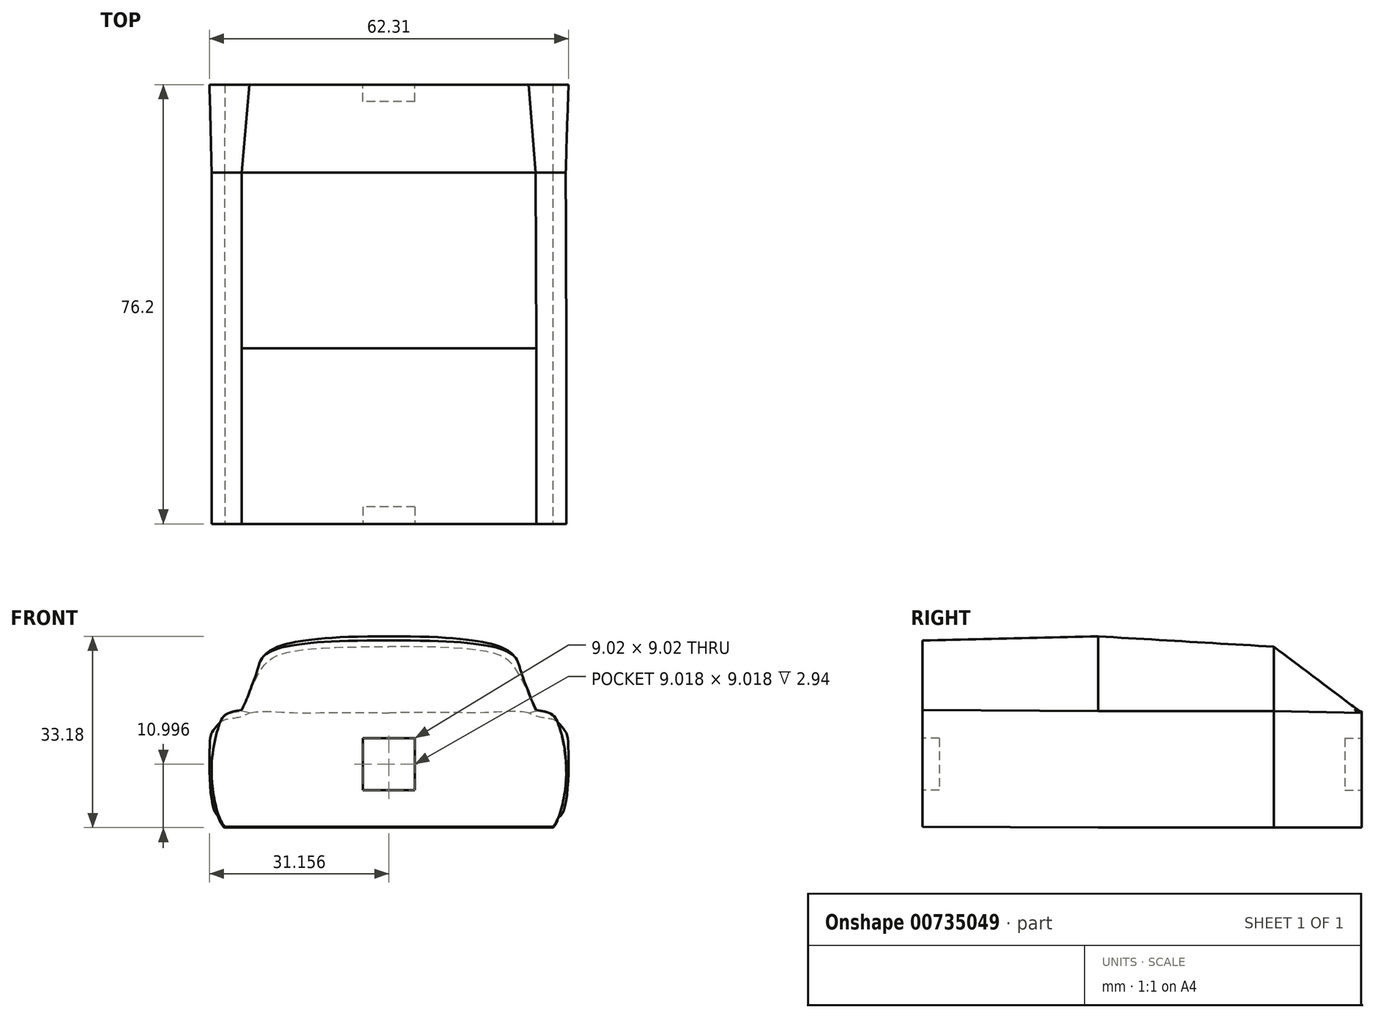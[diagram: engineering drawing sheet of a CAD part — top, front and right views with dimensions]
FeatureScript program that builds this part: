
annotation { "Feature Type Name" : "Feature", "Feature Type Description" : "" }
export const myFeature = defineFeature(function(context is Context, id is Id, definition is map)
    precondition{}
    {
        {
            var Q0;
            Q0=qCreatedBy(makeId("Front.planeOp"),FACE);
            var sketch = newSketch(context, id + "F0", { "sketchPlane" : qUnion([Q0])});
            skLineSegment(sketch, "E0", {"start": v(0, -183.1) * mm, "end": v(448.71, -183.1) * mm});
            skLineSegment(sketch, "E1", {"start": v(0, 369.77) * mm, "end": v(0, -183.1) * mm});
            skFitSpline(sketch, "E2", {"points": [v(448.71, -183.1) * mm, v(474.16, -183.1) * mm, v(512.73, -32.97) * mm, v(489.93, 114.17) * mm, v(425.94, 154.21) * mm], "startDerivative": vector(218.59, -88.61) * mm, "endDerivative": vector(-639.63, 77.65) * mm});
            skFitSpline(sketch, "E3", {"points": [v(425.94, 154.21) * mm, v(403.5, 206.57) * mm, v(378.22, 275.5) * mm, v(362.13, 312.27) * mm, v(0, 369.77) * mm], "startDerivative": vector(-217.52, 427.03) * mm, "endDerivative": vector(-1727.63, -7.94) * mm});
            skFitSpline(sketch, "E4.MirrorCS", {"points": [v(-448.71, -183.1) * mm, v(-474.16, -183.1) * mm, v(-512.73, -32.97) * mm, v(-489.93, 114.17) * mm, v(-425.94, 154.21) * mm], "startDerivative": vector(-218.59, -88.61) * mm, "endDerivative": vector(639.63, 77.65) * mm});
            skLineSegment(sketch, "E5.MirrorCS", {"start": v(0, -183.1) * mm, "end": v(-448.71, -183.1) * mm});
            skFitSpline(sketch, "E6.MirrorCS", {"points": [v(-425.94, 154.21) * mm, v(-403.5, 206.57) * mm, v(-378.22, 275.5) * mm, v(-362.13, 312.27) * mm, v(0, 369.77) * mm], "startDerivative": vector(217.52, 427.03) * mm, "endDerivative": vector(1727.63, -7.94) * mm});
            skLineSegment(sketch, "E7", {"start": v(-474.16, -183.1) * mm, "end": v(-448.71, -183.1) * mm});
            skLineSegment(sketch, "E8", {"start": v(448.71, -183.1) * mm, "end": v(474.16, -183.1) * mm});
            skSolve(sketch);
        }
        {
            var Q0;
            Q0=qCreatedBy(makeId("Front.planeOp"),FACE);
            cPlane(context, id + "F1", {"entities" : qUnion([Q0]), "cplaneType" : CPlaneType.OFFSET, "offset" : 508 * mm, "width" : 152.4 * mm, "height" : 152.4 * mm});
        }
        {
            var Q0;
            Q0=qCreatedBy(makeId("Front.planeOp"),FACE);
            cPlane(context, id + "F2", {"entities" : qUnion([Q0]), "cplaneType" : CPlaneType.OFFSET, "offset" : 508 * mm, "oppositeDirection" : true, "width" : 152.4 * mm, "height" : 152.4 * mm});
        }
        {
            var Q0;
            Q0=qCreatedBy(id+"F2.planeOp",FACE);
            var sketch = newSketch(context, id + "F3", { "sketchPlane" : qUnion([Q0])});
            skLineSegment(sketch, "E9", {"start": v(-0.85, -183.1) * mm, "end": v(447, -183.1) * mm});
            skLineSegment(sketch, "E10", {"start": v(-0.85, 339.88) * mm, "end": v(-0.85, -183.1) * mm});
            skFitSpline(sketch, "E11", {"points": [v(447, -183.1) * mm, v(474.16, -183.1) * mm, v(511.02, -32.97) * mm, v(488.22, 114.17) * mm, v(424.23, 154.21) * mm], "startDerivative": vector(218.59, -88.61) * mm, "endDerivative": vector(-639.63, 77.65) * mm});
            skFitSpline(sketch, "E12", {"points": [v(424.23, 154.21) * mm, v(401.78, 206.57) * mm, v(379.75, 253.63) * mm, v(351.9, 293.8) * mm, v(-0.85, 339.88) * mm], "startDerivative": vector(-217.52, 427.03) * mm, "endDerivative": vector(-1727.63, -7.94) * mm});
            skFitSpline(sketch, "E13.MirrorCS", {"points": [v(-448.71, -183.1) * mm, v(-475.87, -183.1) * mm, v(-512.73, -32.97) * mm, v(-489.93, 114.17) * mm, v(-425.94, 154.21) * mm], "startDerivative": vector(-218.59, -88.61) * mm, "endDerivative": vector(639.63, 77.65) * mm});
            skLineSegment(sketch, "E14.MirrorCS", {"start": v(-0.85, -183.1) * mm, "end": v(-448.71, -183.1) * mm});
            skFitSpline(sketch, "E15.MirrorCS", {"points": [v(-425.94, 154.21) * mm, v(-403.5, 206.57) * mm, v(-381.46, 253.63) * mm, v(-353.6, 293.8) * mm, v(-0.85, 339.88) * mm], "startDerivative": vector(217.52, 427.03) * mm, "endDerivative": vector(1727.63, -7.94) * mm});
            skLineSegment(sketch, "E16", {"start": v(-475.87, -183.1) * mm, "end": v(-448.71, -183.1) * mm});
            skLineSegment(sketch, "E17", {"start": v(447, -183.1) * mm, "end": v(474.16, -183.1) * mm});
            skSolve(sketch);
        }
        {
            var Q0;
            Q0=qCreatedBy(id+"F1.planeOp",FACE);
            var sketch = newSketch(context, id + "F4", { "sketchPlane" : qUnion([Q0])});
            skLineSegment(sketch, "E18", {"start": v(0, -180.47) * mm, "end": v(448.71, -180.47) * mm});
            skLineSegment(sketch, "E19", {"start": v(0, 357.9) * mm, "end": v(0, -180.47) * mm});
            skFitSpline(sketch, "E20", {"points": [v(448.71, -180.47) * mm, v(474.16, -180.47) * mm, v(512.73, -30.33) * mm, v(489.93, 116.8) * mm, v(425.94, 156.85) * mm], "startDerivative": vector(218.59, -88.61) * mm, "endDerivative": vector(-639.63, 77.65) * mm});
            skFitSpline(sketch, "E21", {"points": [v(425.94, 156.85) * mm, v(403.5, 209.2) * mm, v(380.6, 271.65) * mm, v(367.32, 306.69) * mm, v(0, 357.9) * mm], "startDerivative": vector(-217.52, 427.03) * mm, "endDerivative": vector(-1727.63, -7.94) * mm});
            skFitSpline(sketch, "E22.MirrorCS", {"points": [v(-448.71, -180.47) * mm, v(-474.16, -180.47) * mm, v(-512.73, -30.33) * mm, v(-489.93, 116.8) * mm, v(-425.94, 156.85) * mm], "startDerivative": vector(-218.59, -88.61) * mm, "endDerivative": vector(639.63, 77.65) * mm});
            skLineSegment(sketch, "E23.MirrorCS", {"start": v(0, -180.47) * mm, "end": v(-448.71, -180.47) * mm});
            skFitSpline(sketch, "E24.MirrorCS", {"points": [v(-425.94, 156.85) * mm, v(-403.5, 209.2) * mm, v(-380.6, 271.65) * mm, v(-367.32, 306.69) * mm, v(0, 357.9) * mm], "startDerivative": vector(217.52, 427.03) * mm, "endDerivative": vector(1727.63, -7.94) * mm});
            skLineSegment(sketch, "E25", {"start": v(-474.16, -180.47) * mm, "end": v(-448.71, -180.47) * mm});
            skLineSegment(sketch, "E26", {"start": v(448.71, -180.47) * mm, "end": v(474.16, -180.47) * mm});
            skSolve(sketch);
        }
        {
            var Q0;
            Q0=qCreatedBy(makeId("Front.planeOp"),FACE);
            cPlane(context, id + "F5", {"entities" : qUnion([Q0]), "cplaneType" : CPlaneType.OFFSET, "offset" : 762 * mm, "oppositeDirection" : true, "width" : 152.4 * mm, "height" : 152.4 * mm});
        }
        {
            var Q0;
            Q0=qCreatedBy(makeId("Front.planeOp"),FACE);
            cPlane(context, id + "F6", {"entities" : qUnion([Q0]), "cplaneType" : CPlaneType.OFFSET, "offset" : 762 * mm, "oppositeDirection" : true, "width" : 152.4 * mm, "height" : 152.4 * mm});
        }
        {
            var Q0;
            Q0=qCreatedBy(id+"F6.planeOp",FACE);
            var sketch = newSketch(context, id + "F7", { "sketchPlane" : qUnion([Q0])});
            skLineSegment(sketch, "E27", {"start": v(0.16, 148.97) * mm, "end": v(0.16, -183.2) * mm});
            skFitSpline(sketch, "E28.MirrorCS", {"points": [v(-448.56, -183.2) * mm, v(-474, -183.2) * mm, v(-485.4, -157.86) * mm, v(-504.22, -136.35) * mm, v(-516.76, 73.53) * mm, v(-508.8, 96.48) * mm, v(-478.43, 127.41) * mm, v(-403.28, 148.97) * mm], "startDerivative": vector(-218.59, -88.61) * mm, "endDerivative": vector(559.4, 332.46) * mm});
            skLineSegment(sketch, "E29.MirrorCS", {"start": v(0.16, -183.2) * mm, "end": v(-448.56, -183.2) * mm});
            skLineSegment(sketch, "E30", {"start": v(-474, -183.2) * mm, "end": v(-448.56, -183.2) * mm});
            skFitSpline(sketch, "E31", {"points": [v(-403.28, 148.97) * mm, v(-296.35, 149.8) * mm, v(-130.95, 149.8) * mm, v(0.16, 148.97) * mm], "startDerivative": vector(415.6, 70.52) * mm, "endDerivative": vector(425.94, 0) * mm});
            skLineSegment(sketch, "E32.MirrorCS", {"start": v(474.31, -183.2) * mm, "end": v(448.87, -183.2) * mm});
            skFitSpline(sketch, "E33.MirrorCS", {"points": [v(448.87, -183.2) * mm, v(474.31, -183.2) * mm, v(485.71, -157.86) * mm, v(504.54, -136.35) * mm, v(517.08, 73.53) * mm, v(509.12, 96.48) * mm, v(478.74, 127.41) * mm, v(403.6, 148.97) * mm], "startDerivative": vector(218.59, -88.61) * mm, "endDerivative": vector(-559.4, 332.46) * mm});
            skFitSpline(sketch, "E34.MirrorCS", {"points": [v(403.6, 148.97) * mm, v(296.67, 149.8) * mm, v(131.27, 149.8) * mm, v(0.16, 148.97) * mm], "startDerivative": vector(-415.6, 70.52) * mm, "endDerivative": vector(-425.94, 0) * mm});
            skLineSegment(sketch, "E35.MirrorCS", {"start": v(0.16, -183.2) * mm, "end": v(448.87, -183.2) * mm});
            skSolve(sketch);
        }
        {
            var Q0;
            Q0=qCreatedBy(id+"F5.planeOp",FACE);
            var sketch = newSketch(context, id + "F8", { "sketchPlane" : qUnion([Q0])});
            skLineSegment(sketch, "E36.bottom", {"start": v(75.3, 75.3) * mm, "end": v(-75, 75.3) * mm});
            skLineSegment(sketch, "E36.top", {"start": v(75.3, -75) * mm, "end": v(-75, -75) * mm});
            skLineSegment(sketch, "E36.left", {"start": v(75.3, 75.3) * mm, "end": v(75.3, -75) * mm});
            skLineSegment(sketch, "E36.right", {"start": v(-75, 75.3) * mm, "end": v(-75, -75) * mm});
            skPoint(sketch, "E36.middle", {"position": v(0.15, 0.15) * mm});
            skSolve(sketch);
        }
        {
            var Q0;
            Q0=makeQuery(id+"F7.imprint","IMPRINT",FACE,{"disambiguationData":[TD([[makeQuery(id+"F7.imprint","IMPRINT",EDGE,{"derivedFrom":sQuery(id+"F7.wireOp",EDGE,"E27")}),-1.0]])]});
            var Q1;
            Q1=makeQuery(id+"F3.imprint","IMPRINT",FACE,{"disambiguationData":[TD([[makeQuery(id+"F3.imprint","IMPRINT",EDGE,{"derivedFrom":sQuery(id+"F3.wireOp",EDGE,"E10")}),-1.0]])]});
            loft(context, id + "F9", {"sheetProfilesArray" : [{ "sheetProfileEntities" : qUnion([Q0]) }, { "sheetProfileEntities" : qUnion([Q1]) }]});
        }
        {
            var Q1;
            Q1=makeQuery(id+"F7.imprint","IMPRINT",FACE,{"disambiguationData":[TD([[makeQuery(id+"F7.imprint","IMPRINT",EDGE,{"derivedFrom":sQuery(id+"F7.wireOp",EDGE,"E27")}),1.0]])]});
            var Q2;
            Q2=makeQuery(id+"F3.imprint","IMPRINT",FACE,{"disambiguationData":[TD([[makeQuery(id+"F3.imprint","IMPRINT",EDGE,{"derivedFrom":sQuery(id+"F3.wireOp",EDGE,"E9")}),1.0]])]});
            loft(context, id + "F10", {"operationType" : NewBodyOperationType.ADD, "sheetProfilesArray" : [{ "sheetProfileEntities" : qUnion([Q1]) }, { "sheetProfileEntities" : qUnion([Q2]) }]});
        }
        {
            var Q1;
            Q1=makeQuery(id+"F3.imprint","IMPRINT",FACE,{"disambiguationData":[TD([[makeQuery(id+"F3.imprint","IMPRINT",EDGE,{"derivedFrom":sQuery(id+"F3.wireOp",EDGE,"E10")}),-1.0]])]});
            var Q2;
            Q2=makeQuery(id+"F0.imprint","IMPRINT",FACE,{"disambiguationData":[TD([[makeQuery(id+"F0.imprint","IMPRINT",EDGE,{"derivedFrom":sQuery(id+"F0.wireOp",EDGE,"E1")}),-1.0]])]});
            loft(context, id + "F11", {"operationType" : NewBodyOperationType.ADD, "sheetProfilesArray" : [{ "sheetProfileEntities" : qUnion([Q1]) }, { "sheetProfileEntities" : qUnion([Q2]) }]});
        }
        {
            var Q1;
            Q1=makeQuery(id+"F3.imprint","IMPRINT",FACE,{"disambiguationData":[TD([[makeQuery(id+"F3.imprint","IMPRINT",EDGE,{"derivedFrom":sQuery(id+"F3.wireOp",EDGE,"E9")}),1.0]])]});
            var Q2;
            Q2=makeQuery(id+"F0.imprint","IMPRINT",FACE,{"disambiguationData":[TD([[makeQuery(id+"F0.imprint","IMPRINT",EDGE,{"derivedFrom":sQuery(id+"F0.wireOp",EDGE,"E0")}),1.0]])]});
            loft(context, id + "F12", {"operationType" : NewBodyOperationType.ADD, "sheetProfilesArray" : [{ "sheetProfileEntities" : qUnion([Q1]) }, { "sheetProfileEntities" : qUnion([Q2]) }]});
        }
        {
            var Q1;
            Q1=makeQuery(id+"F0.imprint","IMPRINT",FACE,{"disambiguationData":[TD([[makeQuery(id+"F0.imprint","IMPRINT",EDGE,{"derivedFrom":sQuery(id+"F0.wireOp",EDGE,"E1")}),-1.0]])]});
            var Q2;
            Q2=makeQuery(id+"F4.imprint","IMPRINT",FACE,{"disambiguationData":[TD([[makeQuery(id+"F4.imprint","IMPRINT",EDGE,{"derivedFrom":sQuery(id+"F4.wireOp",EDGE,"E19")}),-1.0]])]});
            loft(context, id + "F13", {"operationType" : NewBodyOperationType.ADD, "sheetProfilesArray" : [{ "sheetProfileEntities" : qUnion([Q1]) }, { "sheetProfileEntities" : qUnion([Q2]) }]});
        }
        {
            var Q1;
            Q1=makeQuery(id+"F0.imprint","IMPRINT",FACE,{"disambiguationData":[TD([[makeQuery(id+"F0.imprint","IMPRINT",EDGE,{"derivedFrom":sQuery(id+"F0.wireOp",EDGE,"E0")}),1.0]])]});
            var Q2;
            Q2=makeQuery(id+"F4.imprint","IMPRINT",FACE,{"disambiguationData":[TD([[makeQuery(id+"F4.imprint","IMPRINT",EDGE,{"derivedFrom":sQuery(id+"F4.wireOp",EDGE,"E18")}),1.0]])]});
            loft(context, id + "F14", {"operationType" : NewBodyOperationType.ADD, "sheetProfilesArray" : [{ "sheetProfileEntities" : qUnion([Q1]) }, { "sheetProfileEntities" : qUnion([Q2]) }]});
        }
        {
            var Q0;
            Q0 = qSketchRegion(id + "F8", true);
            extrude(context, id + "F15", {"entities" : qUnion([Q0]), "operationType" : NewBodyOperationType.REMOVE, "depth" : 49 * mm, "offsetDistance" : 25 * mm});
        }
        {
            var Q0;
            Q0=qCreatedBy(id+"F1.planeOp",FACE);
            var sketch = newSketch(context, id + "F16", { "sketchPlane" : qUnion([Q0])});
            skLineSegment(sketch, "E37.bottom", {"start": v(75.25, 75.25) * mm, "end": v(-75.05, 75.25) * mm});
            skLineSegment(sketch, "E37.top", {"start": v(75.25, -75.05) * mm, "end": v(-75.05, -75.05) * mm});
            skLineSegment(sketch, "E37.left", {"start": v(75.25, 75.25) * mm, "end": v(75.25, -75.05) * mm});
            skLineSegment(sketch, "E37.right", {"start": v(-75.05, 75.25) * mm, "end": v(-75.05, -75.05) * mm});
            skPoint(sketch, "E37.middle", {"position": v(0.1, 0.1) * mm});
            skSolve(sketch);
        }
        {
            var Q0;
            Q0 = qSketchRegion(id + "F16", true);
            extrude(context, id + "F17", {"entities" : qUnion([Q0]), "operationType" : NewBodyOperationType.REMOVE, "oppositeDirection" : true, "depth" : 49 * mm, "offsetDistance" : 25 * mm});
        }
        {
            var Q0;
            Q0=makeQuery(id+"F9.opLoft","SWEPT_BODY",BODY,{"disambiguationData":[OSD([makeQuery(id+"F3.imprint","IMPRINT",FACE,{"disambiguationData":[TD([[makeQuery(id+"F3.imprint","IMPRINT",EDGE,{"derivedFrom":sQuery(id+"F3.wireOp",EDGE,"E10")}),-1.0]])]}),makeQuery(id+"F7.imprint","IMPRINT",FACE,{"disambiguationData":[TD([[makeQuery(id+"F7.imprint","IMPRINT",EDGE,{"derivedFrom":sQuery(id+"F7.wireOp",EDGE,"E27")}),-1.0]])]})])]});
            var Q1;
            Q1=qCreatedBy(makeId("Origin.pointOp"),VERTEX);
            var Q2;
            Q2=qCreatedBy(makeId("Origin.pointOp"),VERTEX);
            transform(context, id + "F18", {"entities" : qUnion([Q0]), "transformType" : TransformType.SCALE_UNIFORMLY, "scale" : 0.06, "scalePoint" : qUnion([Q2]), "makeCopy" : false});
        }
    });
